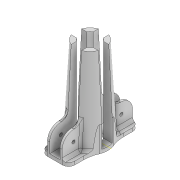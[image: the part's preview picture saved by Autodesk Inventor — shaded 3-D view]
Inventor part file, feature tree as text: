
AUTODESK INVENTOR PART (.ipt)
format: ipt  version: 2021.3 (Build 253353000, 353)  size: 438,272 bytes
history: native  units: mm
features: extrude x7, fillet x5, sketch x4, draft x1
ambient origin geometry x8: Origin, YZ Plane, XZ Plane, XY Plane, X Axis, Y Axis, Z Axis, Center Point
bodies: Solid1 (feature_tree)
feature tree (17):
  sketch  "Sketch1"  dims[d0=7.6mm d2=28.6mm d3=122.475mm d4=0.0mm]
  extrude  "Extrusion1"  Depth=122.475mm TaperAngle=0.0deg
  sketch  "Sketch2"  dims[d15=5.0mm d16=0.0mm d19=31.7mm d20=0.0mm]
  extrude  "Extrusion2"  Depth=31.7mm TaperAngle=0.0deg
  extrude  "Extrusion3"  TaperAngle=0.0deg  [1 undecoded]
  extrude  "Extrusion5"  Depth=10.0mm
  fillet  "Fillet2"  Radius=51.3mm
  sketch  "Sketch4"  dims[d30=31.7mm d31=0.0mm d32=0.0mm]
  extrude  "Extrusion8"  Depth=10.0mm
  extrude  "Extrusion6"  Depth=10.0mm
  fillet  "Fillet3"  Radius=3.2mm
  extrude  "Extrusion9"  TaperAngle=0.0deg  [1 undecoded]
  fillet  "Fillet7"  Radius=7.6mm
  draft  "FaceDraft4"
  fillet  "Fillet8"  Radius=15.7mm
  fillet  "Fillet9"  Radius=15.7mm
  sketch  "Sketch7"  dims[d34=9.0mm d38=20.0mm d41=51.3mm d42=51.3mm d43=37.0mm d44=3.2mm d45=0.0mm d46=7.6mm d47=15.7mm d48=15.7mm d49=4.65mm d50=0.0mm d51=0.0mm d52=17.0mm d56=7.6mm d57=7.6mm d58=0.0mm d59=0.0mm d60=16.3mm d61=42.5mm d66=5.0mm d67=0.0mm d68=52.0mm d69=0.523599mm d70=50.0mm d71=4.0mm d72=10.0mm]
note: 2 required parameter values undecoded (feature->parameter linkage not recoverable at this tier; creation-order binding heuristic only, values carry confidence <= 0.55)
